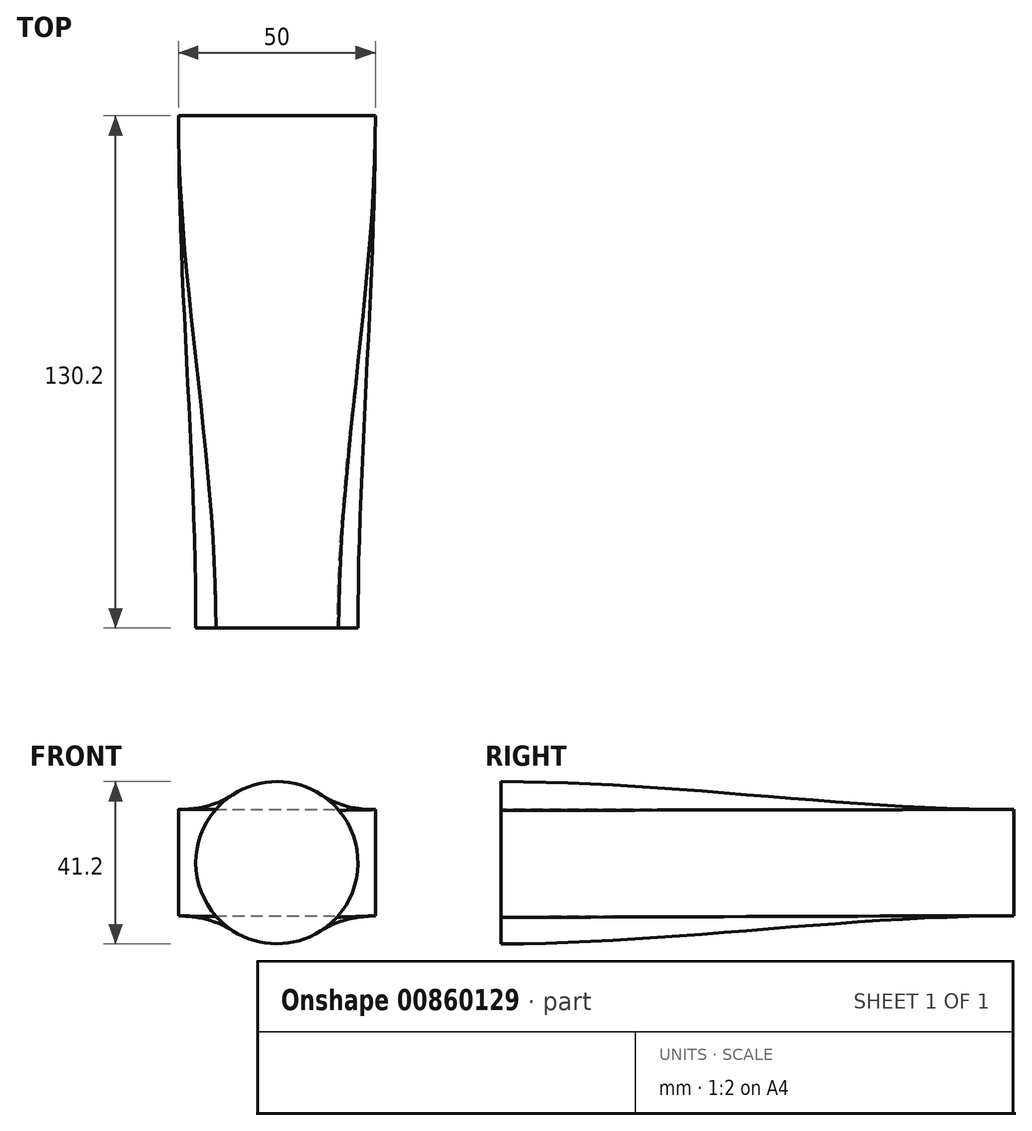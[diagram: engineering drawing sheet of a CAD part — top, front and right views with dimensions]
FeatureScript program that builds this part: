
annotation { "Feature Type Name" : "Feature", "Feature Type Description" : "" }
export const myFeature = defineFeature(function(context is Context, id is Id, definition is map)
    precondition{}
    {
        {
            var Q0;
            Q0=qCreatedBy(makeId("Front.planeOp"),FACE);
            cPlane(context, id + "F0", {"entities" : qUnion([Q0]), "cplaneType" : CPlaneType.OFFSET, "offset" : 130.2 * mm, "width" : 150 * mm, "height" : 150 * mm});
        }
        {
            var Q0;
            Q0=qCreatedBy(makeId("Front.planeOp"),FACE);
            var sketch = newSketch(context, id + "F1", { "sketchPlane" : qUnion([Q0])});
            skLineSegment(sketch, "E0.bottom", {"start": v(-25, 13.5) * mm, "end": v(25, 13.5) * mm});
            skLineSegment(sketch, "E0.top", {"start": v(-25, -13.5) * mm, "end": v(25, -13.5) * mm});
            skLineSegment(sketch, "E0.left", {"start": v(-25, 13.5) * mm, "end": v(-25, -13.5) * mm});
            skLineSegment(sketch, "E0.right", {"start": v(25, 13.5) * mm, "end": v(25, -13.5) * mm});
            skSolve(sketch);
        }
        {
            var Q0;
            Q0=qCreatedBy(id+"F0.planeOp",FACE);
            var sketch = newSketch(context, id + "F2", { "sketchPlane" : qUnion([Q0])});
            skArc(sketch, "E1", {"start": v(-15.49, 13.58) * mm, "mid": v(-20.6, -0.08) * mm, "end": v(-15.38, -13.7) * mm});
            skArc(sketch, "E2", {"start": v(-15.38, -13.7) * mm, "mid": v(-0.1, -20.6) * mm, "end": v(15.24, -13.86) * mm});
            skArc(sketch, "E3", {"start": v(15.24, -13.86) * mm, "mid": v(20.6, -0.36) * mm, "end": v(15.7, 13.33) * mm});
            skArc(sketch, "E4", {"start": v(15.7, 13.33) * mm, "mid": v(0.17, 20.6) * mm, "end": v(-15.49, 13.58) * mm});
            skSolve(sketch);
        }
        {
            var Q0;
            Q0=makeQuery(id+"F1.imprint","IMPRINT",FACE,{"disambiguationData":[TD([[makeQuery(id+"F1.imprint","IMPRINT",EDGE,{"derivedFrom":sQuery(id+"F1.wireOp",EDGE,"E0.bottom")}),-1.0]])]});
            var Q1;
            Q1=makeQuery(id+"F2.imprint","IMPRINT",FACE,{"disambiguationData":[TD([[makeQuery(id+"F2.imprint","IMPRINT",EDGE,{"derivedFrom":sQuery(id+"F2.wireOp",EDGE,"E1")}),1.0]])]});
            loft(context, id + "F3", {"startCondition" : LoftEndDerivativeType.NORMAL_TO_PROFILE, "startMagnitude" : 1, "endCondition" : LoftEndDerivativeType.NORMAL_TO_PROFILE, "endMagnitude" : 1, "sheetProfilesArray" : [{ "sheetProfileEntities" : qUnion([Q0]) }, { "sheetProfileEntities" : qUnion([Q1]) }]});
        }
    });
